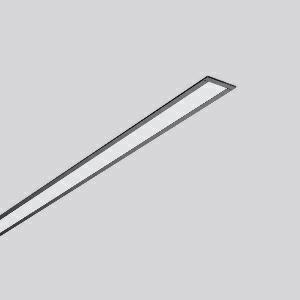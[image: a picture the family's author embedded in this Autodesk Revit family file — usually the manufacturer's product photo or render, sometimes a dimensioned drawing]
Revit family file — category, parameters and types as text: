
# Revit family: less_is_more_27_312178_003_1_76_5c99
name_source: partatom
category: Lighting Fixtures
units: mm (PartAtom-declared; Revit-internal decimal feet)

## family parameters
Cut with Voids When Loaded = No
Host = Face
Light Source = No
Part Type = Normal
Room Calculation Point = No
Round Connector Dimension = Use Diameter
Shared = No

## types (1)
- LESS IS MORE 27 (1 x LED Modul 840, 2400 lm, 4000)
    Apparent Load = 39 VA
    CIE Flux Codes = 48 79 96 100 100
    Color Rendering = 80
    Color Temperature = 4000
    Default Elevation = 1800 mm
    Description = Series: LESS IS MORE 27
Recessed ceiling and wall luminaire with slim design. Housing: extruded aluminium profile, powder-coated. End cap aluminium powder-coated. Diffuser made of non-yellowing plastic (PMMA), opal. Suitable for Recessed ceiling mounting, wall (recessed). External driver with connecting cable. 
Colour: deep black, matt (RAL 9005)
Length: 1514 mm
Width: 38 mm
Height: 2 mm
Cut-out length: 1506 mm
Cut-out width: 30 mm
Recess height: 45-60 mm
Luminaire: recess height: 37 mm
Lamp: LED
Socket: without socket
Colour temperature: 4000K
Colour rendering index (CRI): 82
System power: 39 W
Rated luminous flux: 2400 lm
Luminous efficiency: 62 lm/W
Control gear: Voltage converter, DALI dim.
Protection class: II
Type of protection: IP 20
    Height = 0 mm  [stored 0 ft]
    Lamp = 1 x LED Modul 840
    Lamp Light Flux = 2400 lm
    Lamp count = 1
    Length = 1514 mm
    Lifetime = 50000 h
    Luminous efficacy = 62 lm/W
    Manufacturer = RZB
    ModVariant = No
    Model = 312178.003.1.76
    Mounting Place = Ceiling, Wall
    Mounting Type = Recessed
    Number of Poles = 1
    OnlyDefault = Yes
    Power Factor = 1
    Product Name = LESS IS MORE 27
    Product group = Recessed LED linear luminaires
    ProductGroupID = 407
    Protection Class = Protection class II
    Protection Degree = IP 20
    RLX_Detail_Level = 1
    RLX_Emergency_Light_Flux = 0 lm
    RLX_Emergency_Type = 0
    RLX_Emergency_Type_DB = No
    RlxData = <blob elided: 26153 chars, md5=83a24244>
    Socket = socket
    Standby Power = 0 W
    System Light Flux = 2400 lm
    System Power = 39 W
    Type Comments = Product without accessories
    Type Image = 312176.003.jpg
    URL = http://relux.com
    VarID = ---
    Voltage = 230 V
    Voltage Range = 220-240 V
    Weight = 0.00 kg
    Width = 38 mm

note: [stored X ft] marks values corroborated as IEEE doubles in the binary element streams (Revit-internal decimal feet)

## geometry (parser evidence)
native form markers: Blend x4, Sweep x13
no freeform markers — native parametric forms only
